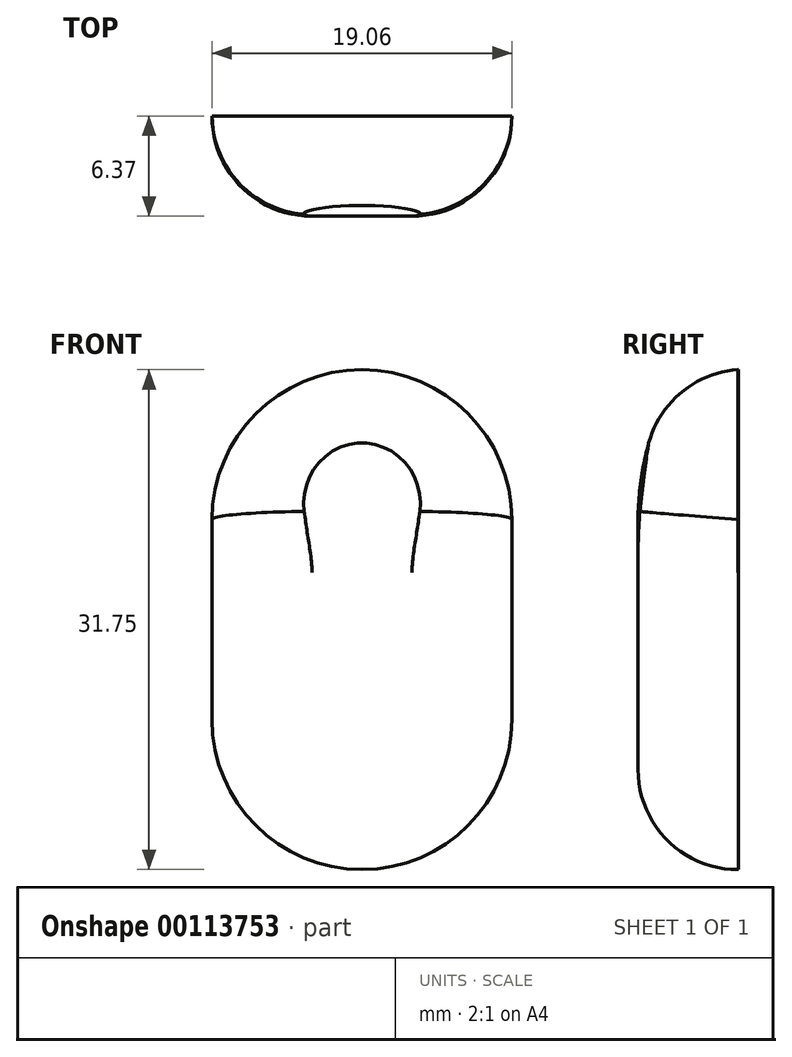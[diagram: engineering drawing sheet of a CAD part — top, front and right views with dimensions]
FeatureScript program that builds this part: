
annotation { "Feature Type Name" : "Feature", "Feature Type Description" : "" }
export const myFeature = defineFeature(function(context is Context, id is Id, definition is map)
    precondition{}
    {
        {
            var Q0;
            Q0=qCreatedBy(makeId("Front.planeOp"),FACE);
            var sketch = newSketch(context, id + "F0", { "sketchPlane" : qUnion([Q0])});
            skLineSegment(sketch, "E0.bottom", {"start": v(25.4, 50.8) * mm, "end": v(-25.4, 50.8) * mm});
            skLineSegment(sketch, "E0.top", {"start": v(25.4, -50.8) * mm, "end": v(-25.4, -50.8) * mm});
            skLineSegment(sketch, "E0.left", {"start": v(25.4, 50.8) * mm, "end": v(25.4, -50.8) * mm});
            skLineSegment(sketch, "E0.right", {"start": v(-25.4, 50.8) * mm, "end": v(-25.4, -50.8) * mm});
            skPoint(sketch, "E0.middle", {"position": v(0, 0) * mm});
            skSolve(sketch);
        }
        {
            var Q0;
            Q0=qSketchRegion(id+"F0",true);
            extrude(context, id + "F1", {"entities" : qUnion([Q0]), "depth" : 12.7 * mm});
        }
        {
            var Q0;
            Q0=qCreatedBy(makeId("Top.planeOp"),FACE);
            var sketch = newSketch(context, id + "F2", { "sketchPlane" : qUnion([Q0])});
            skLineSegment(sketch, "E1", {"start": v(25.4, 0) * mm, "end": v(36.1, 0) * mm});
            skLineSegment(sketch, "E2", {"start": v(36.1, 0) * mm, "end": v(25.4, -12.67) * mm});
            skLineSegment(sketch, "E3", {"start": v(25.4, -12.67) * mm, "end": v(25.4, 0) * mm});
            skLineSegment(sketch, "E4.MirrorCS", {"start": v(-36.1, 0) * mm, "end": v(-25.4, -12.67) * mm});
            skLineSegment(sketch, "E5.MirrorCS", {"start": v(-25.4, -12.67) * mm, "end": v(-25.4, 0) * mm});
            skLineSegment(sketch, "E6.MirrorCS", {"start": v(-25.4, 0) * mm, "end": v(-36.1, 0) * mm});
            skSolve(sketch);
        }
        {
            var Q0;
            Q0=qSketchRegion(id+"F2",true);
            extrude(context, id + "F3", {"entities" : qUnion([Q0]), "operationType" : NewBodyOperationType.ADD, "depth" : 101.6 * mm, "symmetric" : true});
        }
        {
            var Q0;
            Q0=qCreatedBy(makeId("Top.planeOp"),FACE);
            var sketch = newSketch(context, id + "F4", { "sketchPlane" : qUnion([Q0])});
            skCircle(sketch, "E7", {"center": v(-31.41, -2.42) * mm, "radius": 1.43 * mm});
            skCircle(sketch, "E8.MirrorC", {"center": v(31.41, -2.42) * mm, "radius": 1.43 * mm});
            skLineSegment(sketch, "E9.bottom", {"start": v(27.18, 1.43) * mm, "end": v(39.9, 1.43) * mm});
            skLineSegment(sketch, "E9.top", {"start": v(27.18, -11.19) * mm, "end": v(39.9, -11.19) * mm});
            skLineSegment(sketch, "E9.left", {"start": v(27.18, 1.43) * mm, "end": v(27.18, -11.19) * mm});
            skLineSegment(sketch, "E9.right", {"start": v(39.9, 1.43) * mm, "end": v(39.9, -11.19) * mm});
            skLineSegment(sketch, "E10.MirrorCS", {"start": v(-27.18, -11.19) * mm, "end": v(-39.9, -11.19) * mm});
            skLineSegment(sketch, "E11.MirrorCS", {"start": v(-39.9, 1.43) * mm, "end": v(-39.9, -11.19) * mm});
            skLineSegment(sketch, "E12.MirrorCS", {"start": v(-27.18, 1.43) * mm, "end": v(-39.9, 1.43) * mm});
            skLineSegment(sketch, "E13.MirrorCS", {"start": v(-27.18, 1.43) * mm, "end": v(-27.18, -11.19) * mm});
            skSolve(sketch);
        }
        {
            var Q0;
            Q0=makeQuery(id+"F4.imprint","IMPRINT",FACE,{"disambiguationData":[TD([[makeQuery(id+"F4.imprint","IMPRINT",EDGE,{"derivedFrom":sQuery(id+"F4.wireOp",EDGE,"E8.MirrorC")}),1.0]])]});
            var Q1;
            Q1=makeQuery(id+"F4.imprint","IMPRINT",FACE,{"disambiguationData":[TD([[makeQuery(id+"F4.imprint","IMPRINT",EDGE,{"derivedFrom":sQuery(id+"F4.wireOp",EDGE,"E7")}),-1.0]])]});
            extrude(context, id + "F5", {"entities" : qUnion([Q0, Q1]), "operationType" : NewBodyOperationType.REMOVE, "oppositeDirection" : true, "depth" : 76.2 * mm, "symmetric" : true});
        }
        {
            var Q0;
            Q0=qCreatedBy(makeId("Front.planeOp"),FACE);
            var sketch = newSketch(context, id + "F6", { "sketchPlane" : qUnion([Q0])});
            skLineSegment(sketch, "E14", {"start": v(-40.53, 38.9) * mm, "end": v(-23.28, 56.16) * mm});
            skLineSegment(sketch, "E15", {"start": v(-23.28, 56.16) * mm, "end": v(-40.53, 56.16) * mm});
            skLineSegment(sketch, "E16", {"start": v(-40.53, 56.16) * mm, "end": v(-40.53, 38.9) * mm});
            skLineSegment(sketch, "E17.MirrorCS", {"start": v(40.53, 56.16) * mm, "end": v(40.53, 38.9) * mm});
            skLineSegment(sketch, "E18.MirrorCS", {"start": v(23.28, 56.16) * mm, "end": v(40.53, 56.16) * mm});
            skLineSegment(sketch, "E19.MirrorCS", {"start": v(40.53, 38.9) * mm, "end": v(23.28, 56.16) * mm});
            skLineSegment(sketch, "E20.MirrorCS", {"start": v(-40.53, -56.16) * mm, "end": v(-40.53, -38.9) * mm});
            skLineSegment(sketch, "E21.MirrorCS", {"start": v(-23.28, -56.16) * mm, "end": v(-40.53, -56.16) * mm});
            skLineSegment(sketch, "E22.MirrorCS", {"start": v(-40.53, -38.9) * mm, "end": v(-23.28, -56.16) * mm});
            skLineSegment(sketch, "E23.MirrorCS", {"start": v(40.53, -38.9) * mm, "end": v(23.28, -56.16) * mm});
            skLineSegment(sketch, "E24.MirrorCS", {"start": v(23.28, -56.16) * mm, "end": v(40.53, -56.16) * mm});
            skLineSegment(sketch, "E25.MirrorCS", {"start": v(40.53, -56.16) * mm, "end": v(40.53, -38.9) * mm});
            skSolve(sketch);
        }
        {
            var Q0;
            Q0=makeQuery(id+"F6.imprint","IMPRINT",FACE,{"disambiguationData":[TD([[makeQuery(id+"F6.imprint","IMPRINT",EDGE,{"derivedFrom":sQuery(id+"F6.wireOp",EDGE,"E17.MirrorCS")}),-1.0]])]});
            var Q1;
            Q1=makeQuery(id+"F6.imprint","IMPRINT",FACE,{"disambiguationData":[TD([[makeQuery(id+"F6.imprint","IMPRINT",EDGE,{"derivedFrom":sQuery(id+"F6.wireOp",EDGE,"E20.MirrorCS")}),-1.0]])]});
            var Q2;
            Q2=makeQuery(id+"F6.imprint","IMPRINT",FACE,{"disambiguationData":[TD([[makeQuery(id+"F6.imprint","IMPRINT",EDGE,{"derivedFrom":sQuery(id+"F6.wireOp",EDGE,"E23.MirrorCS")}),1.0]])]});
            var Q3;
            Q3=makeQuery(id+"F6.imprint","IMPRINT",FACE,{"disambiguationData":[TD([[makeQuery(id+"F6.imprint","IMPRINT",EDGE,{"derivedFrom":sQuery(id+"F6.wireOp",EDGE,"E14")}),1.0]])]});
            extrude(context, id + "F7", {"entities" : qUnion([Q0, Q1, Q2, Q3]), "operationType" : NewBodyOperationType.REMOVE, "endBound" : BoundingType.THROUGH_ALL, "depth" : 25.4 * mm});
        }
        {
            var Q0;
            Q0=makeQuery(id+"F1.opExtrude","CAP_FACE",FACE,{"disambiguationData":[OSD([sQuery(id+"F0.wireOp",EDGE,"E0.bottom"),sQuery(id+"F0.wireOp",EDGE,"E0.top"),sQuery(id+"F0.wireOp",EDGE,"E0.left"),sQuery(id+"F0.wireOp",EDGE,"E0.right")])],"isStart":false});
            var sketch = newSketch(context, id + "F8", { "sketchPlane" : qUnion([Q0])});
            skLineSegment(sketch, "E26.bottom", {"start": v(22.23, 28.57) * mm, "end": v(-22.22, 28.57) * mm});
            skLineSegment(sketch, "E26.top", {"start": v(22.22, -28.58) * mm, "end": v(-22.22, -28.58) * mm});
            skLineSegment(sketch, "E26.left", {"start": v(22.22, 28.57) * mm, "end": v(22.22, -28.58) * mm});
            skLineSegment(sketch, "E26.right", {"start": v(-22.23, 28.57) * mm, "end": v(-22.23, -28.58) * mm});
            skPoint(sketch, "E26.middle", {"position": v(0, 0) * mm});
            skArc(sketch, "E27", {"start": v(22.23, 28.58) * mm, "mid": v(0, 50.8) * mm, "end": v(-22.23, 28.57) * mm});
            skArc(sketch, "E28", {"start": v(-22.23, -28.58) * mm, "mid": v(0, -50.8) * mm, "end": v(22.23, -28.58) * mm});
            skSolve(sketch);
        }
        {
            var Q0;
            Q0=qSketchRegion(id+"F8",true);
            extrude(context, id + "F9", {"entities" : qUnion([Q0]), "operationType" : NewBodyOperationType.ADD, "depth" : 25.4 * mm});
        }
        {
            var Q0;
            Q0=makeQuery(id+"F9.opExtrude","CAP_EDGE",EDGE,{"disambiguationData":[OSD([sQuery(id+"F8.wireOp",EDGE,"E26.left")])],"isStart":false});
            fillet(context, id + "F10", {"entities" : qUnion([Q0]), "radius" : 19.05 * mm, "tangentPropagation" : true, "allowEdgeOverflow" : false});
        }
        {
            var Q0;
            Q0=makeQuery(id+"F9.opExtrude","CAP_FACE",FACE,{"disambiguationData":[OSD([sQuery(id+"F8.wireOp",EDGE,"E26.left"),sQuery(id+"F8.wireOp",EDGE,"E26.right"),sQuery(id+"F8.wireOp",EDGE,"E27"),sQuery(id+"F8.wireOp",EDGE,"E28")])],"isStart":false});
            var sketch = newSketch(context, id + "F11", { "sketchPlane" : qUnion([Q0])});
            skLineSegment(sketch, "E29.left", {"start": v(12.7, 103.58) * mm, "end": v(12.7, 7.15) * mm});
            skLineSegment(sketch, "E29.right", {"start": v(-12.7, 103.58) * mm, "end": v(-12.7, 7.15) * mm});
            skPoint(sketch, "E30.middle", {"position": v(0, 31.75) * mm});
            skLineSegment(sketch, "E31", {"start": v(-12.7, 103.58) * mm, "end": v(12.7, 103.58) * mm});
            skPoint(sketch, "E32.orphan", {"position": v(-12.7, 56.35) * mm});
            skPoint(sketch, "E33.orphan", {"position": v(12.7, 56.35) * mm});
            skLineSegment(sketch, "E34.bottom", {"start": v(9.52, 31.92) * mm, "end": v(-9.52, 31.92) * mm});
            skLineSegment(sketch, "E34.top", {"start": v(9.52, 19.22) * mm, "end": v(-9.52, 19.22) * mm});
            skLineSegment(sketch, "E34.left", {"start": v(9.52, 31.92) * mm, "end": v(9.52, 19.22) * mm});
            skLineSegment(sketch, "E34.right", {"start": v(-9.52, 31.92) * mm, "end": v(-9.52, 19.22) * mm});
            skPoint(sketch, "E34.middle", {"position": v(0, 25.57) * mm});
            skArc(sketch, "E35", {"start": v(-9.52, 19.22) * mm, "mid": v(0, 9.7) * mm, "end": v(9.52, 19.22) * mm});
            skArc(sketch, "E36", {"start": v(9.52, 31.92) * mm, "mid": v(0, 41.44) * mm, "end": v(-9.52, 31.92) * mm});
            skLineSegment(sketch, "E37.top", {"start": v(-12.7, -11.11) * mm, "end": v(12.7, -11.11) * mm});
            skLineSegment(sketch, "E37.left", {"start": v(-12.7, 7.15) * mm, "end": v(-12.7, -11.11) * mm});
            skLineSegment(sketch, "E37.right", {"start": v(12.7, 7.15) * mm, "end": v(12.7, -11.11) * mm});
            skSolve(sketch);
        }
        {
            var Q0;
            Q0=qSketchRegion(id+"F11",true);
            extrude(context, id + "F12", {"entities" : qUnion([Q0]), "operationType" : NewBodyOperationType.REMOVE, "oppositeDirection" : true, "depth" : 6.35 * mm});
        }
        {
            var Q0;
            Q0=makeQuery(id+"F12.boolean.opBoolean","INTERSECT",EDGE,{"derivedFrom":[makeQuery(id+"F10.opFillet","BLEND_FACE",FACE,{"disambiguationData":[OSD([sQuery(id+"F8.wireOp",EDGE,"E26.right")])]}),makeQuery(id+"F12.opExtrude","SWEPT_FACE",FACE,{"disambiguationData":[OSD([sQuery(id+"F11.wireOp",EDGE,"E34.right")])]})]});
            fillet(context, id + "F13", {"entities" : qUnion([Q0]), "radius" : 6.35 * mm, "tangentPropagation" : true, "allowEdgeOverflow" : false});
        }
        {
            var Q0;
            Q0=qCreatedBy(makeId("Top.planeOp"),FACE);
            var sketch = newSketch(context, id + "F14", { "sketchPlane" : qUnion([Q0])});
            skLineSegment(sketch, "E38.bottom", {"start": v(-47.2, 12.7) * mm, "end": v(52.53, 12.7) * mm});
            skLineSegment(sketch, "E38.top", {"start": v(-47.2, -31.73) * mm, "end": v(-43.28, -31.73) * mm});
            skLineSegment(sketch, "E38.left", {"start": v(-47.2, 12.7) * mm, "end": v(-47.2, -31.73) * mm});
            skLineSegment(sketch, "E38.right", {"start": v(52.53, 12.7) * mm, "end": v(52.53, -31.73) * mm});
            skLineSegment(sketch, "E39.bottom", {"start": v(52.53, -56.94) * mm, "end": v(9.64, -56.94) * mm});
            skLineSegment(sketch, "E39.left", {"start": v(52.53, -56.94) * mm, "end": v(52.53, -31.53) * mm});
            skLineSegment(sketch, "E39.right", {"start": v(9.64, -56.94) * mm, "end": v(9.64, -31.73) * mm});
            skLineSegment(sketch, "E40.bottom", {"start": v(-44.68, -56.1) * mm, "end": v(-11, -56.1) * mm});
            skLineSegment(sketch, "E40.left", {"start": v(-44.68, -56.1) * mm, "end": v(-43.28, -31.73) * mm});
            skLineSegment(sketch, "E40.right", {"start": v(-11, -56.1) * mm, "end": v(-9.6, -31.73) * mm});
            skLineSegment(sketch, "E41.trimOffspring", {"start": v(-9.6, -31.73) * mm, "end": v(9.64, -31.73) * mm});
            skSolve(sketch);
        }
        {
            var Q0;
            Q0 = qSketchRegion(id + "F14", true);
            extrude(context, id + "F15", {"entities" : qUnion([Q0]), "operationType" : NewBodyOperationType.REMOVE, "oppositeDirection" : true, "depth" : 127 * mm, "symmetric" : true});
        }
        {
            var Q0;
            Q0=qCreatedBy(makeId("Front.planeOp"),FACE);
            var sketch = newSketch(context, id + "F16", { "sketchPlane" : qUnion([Q0])});
            skArc(sketch, "E42.0", {"start": v(9.52, 31.92) * mm, "mid": v(0, 41.44) * mm, "end": v(-9.52, 31.92) * mm});
            skLineSegment(sketch, "E43.0", {"start": v(-9.52, 31.92) * mm, "end": v(-9.52, 28.57) * mm});
            skLineSegment(sketch, "E43.1", {"start": v(-9.52, 28.57) * mm, "end": v(-9.52, 19.22) * mm});
            skArc(sketch, "E43.2", {"start": v(-9.52, 19.22) * mm, "mid": v(0, 9.7) * mm, "end": v(9.52, 19.22) * mm});
            skLineSegment(sketch, "E43.3", {"start": v(9.52, 31.92) * mm, "end": v(9.52, 28.57) * mm});
            skLineSegment(sketch, "E43.4", {"start": v(9.52, 28.57) * mm, "end": v(9.52, 19.22) * mm});
            skLineSegment(sketch, "E44.bottom", {"start": v(-20.17, 53.94) * mm, "end": v(17.31, 53.94) * mm});
            skLineSegment(sketch, "E44.top", {"start": v(-20.17, -53.75) * mm, "end": v(17.31, -53.75) * mm});
            skLineSegment(sketch, "E44.left", {"start": v(-20.17, 53.94) * mm, "end": v(-20.17, -53.75) * mm});
            skLineSegment(sketch, "E44.right", {"start": v(17.31, 53.94) * mm, "end": v(17.31, -53.75) * mm});
            skSolve(sketch);
        }
        {
            var Q0;
            Q0 = qSketchRegion(id + "F16", true);
            extrude(context, id + "F17", {"entities" : qUnion([Q0]), "operationType" : NewBodyOperationType.REMOVE, "depth" : 50.8 * mm});
        }
    });
